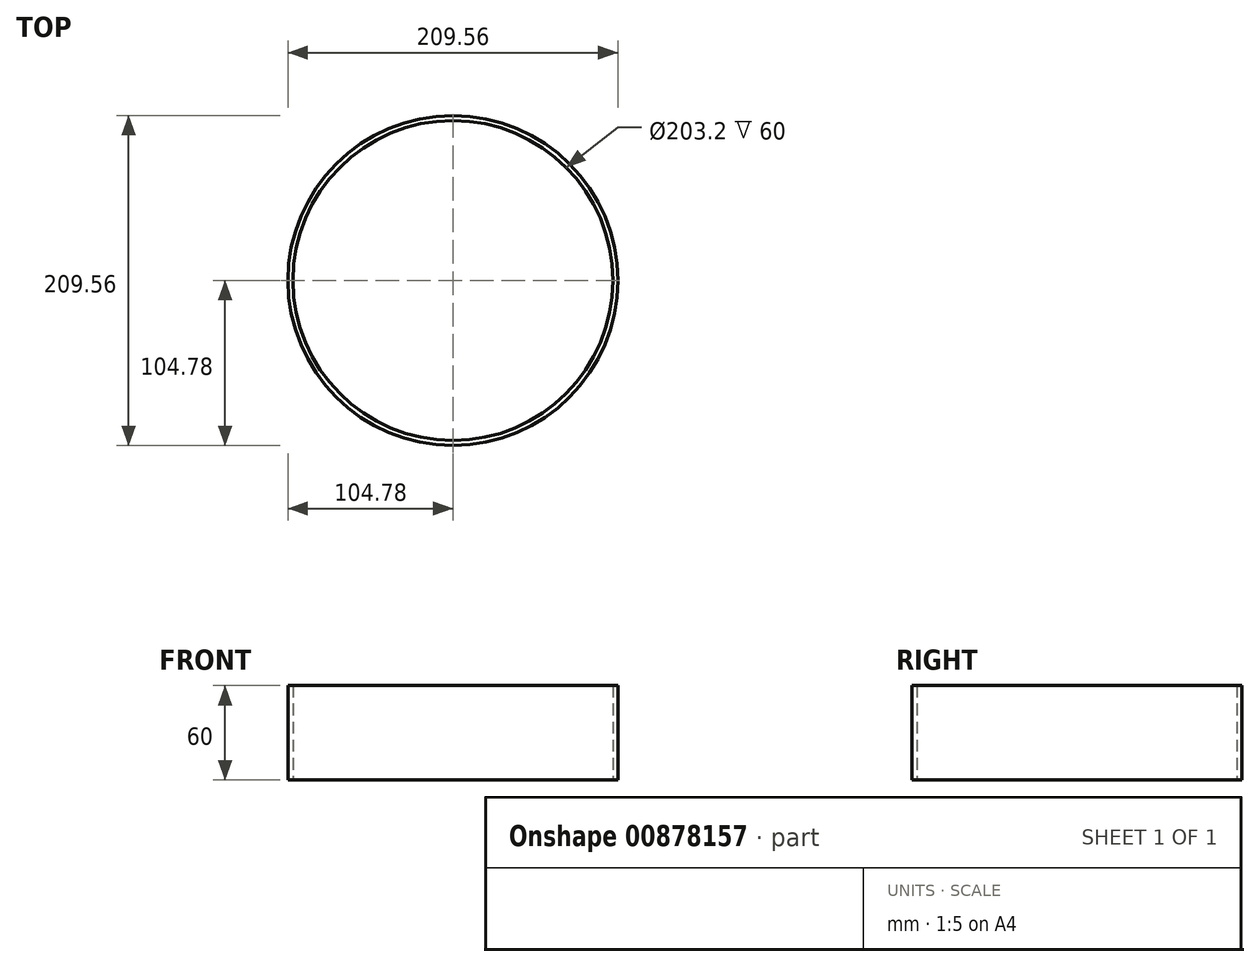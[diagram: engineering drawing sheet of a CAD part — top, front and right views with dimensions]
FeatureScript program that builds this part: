
annotation { "Feature Type Name" : "Feature", "Feature Type Description" : "" }
export const myFeature = defineFeature(function(context is Context, id is Id, definition is map)
    precondition{}
    {
        {
            var Q0;
            Q0=qCreatedBy(makeId("Top.planeOp"),FACE);
            var sketch = newSketch(context, id + "F0", { "sketchPlane" : qUnion([Q0])});
            skCircle(sketch, "E0", {"center": v(0, 0) * mm, "radius": 101.6 * mm});
            skCircle(sketch, "E1.0", {"center": v(0, 0) * mm, "radius": 104.78 * mm});
            skSolve(sketch);
        }
        {
            var Q0;
            Q0 = qSketchRegion(id + "F0", true);
            extrude(context, id + "F1", {"entities" : qUnion([Q0]), "depth" : 60 * mm, "offsetDistance" : 25.4 * mm, "symmetric" : true});
        }
    });
